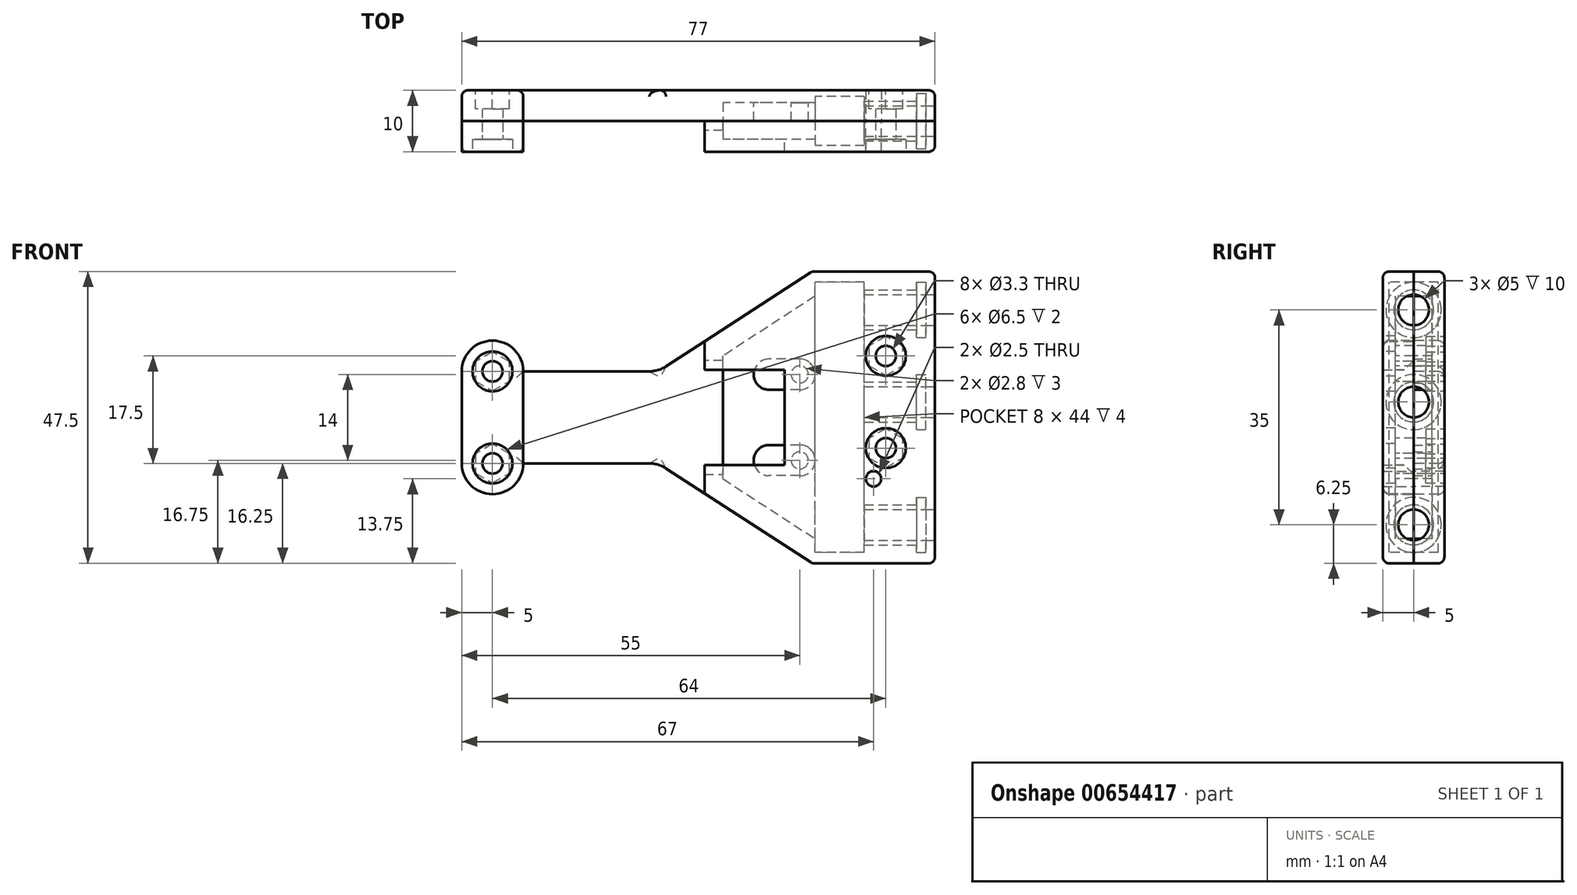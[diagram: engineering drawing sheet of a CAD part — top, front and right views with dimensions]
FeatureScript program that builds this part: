
annotation { "Feature Type Name" : "Feature", "Feature Type Description" : "" }
export const myFeature = defineFeature(function(context is Context, id is Id, definition is map)
    precondition{}
    {
        {
            var Q0;
            Q0=qCreatedBy(makeId("Right.planeOp"),FACE);
            var sketch = newSketch(context, id + "F0", { "sketchPlane" : qUnion([Q0])});
            skCircle(sketch, "E0", {"center": v(0, 17.5) * mm, "radius": 4.5 * mm});
            skCircle(sketch, "E1", {"center": v(0, 17.5) * mm, "radius": 3.25 * mm});
            skCircle(sketch, "E2", {"center": v(0, 2.5) * mm, "radius": 3.25 * mm});
            skCircle(sketch, "E3", {"center": v(0, 2.5) * mm, "radius": 4.5 * mm});
            skCircle(sketch, "E4", {"center": v(0, -17.5) * mm, "radius": 4.5 * mm});
            skCircle(sketch, "E5", {"center": v(0, -17.5) * mm, "radius": 3.25 * mm});
            skCircle(sketch, "E6", {"center": v(0, 17.5) * mm, "radius": 2.5 * mm});
            skCircle(sketch, "E7", {"center": v(0, 2.5) * mm, "radius": 2.5 * mm});
            skCircle(sketch, "E8", {"center": v(0, -17.5) * mm, "radius": 2.5 * mm});
            skLineSegment(sketch, "E9.bottom", {"start": v(5.5, -17.5) * mm, "end": v(-5.5, -17.5) * mm});
            skLineSegment(sketch, "E9.top", {"start": v(5.5, 17.5) * mm, "end": v(-5.5, 17.5) * mm});
            skLineSegment(sketch, "E9.left", {"start": v(5.5, -17.5) * mm, "end": v(5.5, 17.5) * mm});
            skLineSegment(sketch, "E9.right", {"start": v(-5.5, -17.5) * mm, "end": v(-5.5, 17.5) * mm});
            skPoint(sketch, "E9.middle", {"position": v(0, 0) * mm});
            skArc(sketch, "E10", {"start": v(-5.5, 17.5) * mm, "mid": v(0, 23) * mm, "end": v(5.5, 17.5) * mm});
            skArc(sketch, "E11", {"start": v(-5.5, -17.5) * mm, "mid": v(0, -23) * mm, "end": v(5.5, -17.5) * mm});
            skSolve(sketch);
        }
        {
            var Q0;
            {var subQ0=sQuery(id+"F0.wireOp",EDGE,"E9.top");var subQ1=sQuery(id+"F0.wireOp",EDGE,"E1");var subQ2=makeQuery(id+"F0.imprint","INTERSECT",VERTEX,{"disambiguationData":[OD(0.0)],"derivedFrom":[subQ1,subQ0]});Q0=makeQuery(id+"F0.imprint","IMPRINT",FACE,{"disambiguationData":[TD([[makeQuery(id+"F0.imprint","IMPRINT",EDGE,{"disambiguationData":[TD([[subQ2,-1.0]])],"derivedFrom":subQ1}),1.0]])]});}
            var Q1;
            {var subQ0=sQuery(id+"F0.wireOp",EDGE,"E9.top");var subQ1=sQuery(id+"F0.wireOp",EDGE,"E1");var subQ2=makeQuery(id+"F0.imprint","INTERSECT",VERTEX,{"disambiguationData":[OD(0.0)],"derivedFrom":[subQ1,subQ0]});Q1=makeQuery(id+"F0.imprint","IMPRINT",FACE,{"disambiguationData":[TD([[makeQuery(id+"F0.imprint","IMPRINT",EDGE,{"disambiguationData":[TD([[subQ2,1.0]])],"derivedFrom":subQ1}),1.0]])]});}
            var Q2;
            Q2=makeQuery(id+"F0.imprint","IMPRINT",FACE,{"disambiguationData":[TD([[makeQuery(id+"F0.imprint","IMPRINT",EDGE,{"derivedFrom":sQuery(id+"F0.wireOp",EDGE,"E2")}),1.0]])]});
            var Q3;
            {var subQ0=sQuery(id+"F0.wireOp",EDGE,"E9.bottom");var subQ1=sQuery(id+"F0.wireOp",EDGE,"E5");var subQ2=makeQuery(id+"F0.imprint","INTERSECT",VERTEX,{"disambiguationData":[OD(0.0)],"derivedFrom":[subQ1,subQ0]});Q3=makeQuery(id+"F0.imprint","IMPRINT",FACE,{"disambiguationData":[TD([[makeQuery(id+"F0.imprint","IMPRINT",EDGE,{"disambiguationData":[TD([[subQ2,-1.0]])],"derivedFrom":subQ1}),1.0]])]});}
            var Q4;
            {var subQ0=sQuery(id+"F0.wireOp",EDGE,"E9.bottom");var subQ1=sQuery(id+"F0.wireOp",EDGE,"E5");var subQ2=makeQuery(id+"F0.imprint","INTERSECT",VERTEX,{"disambiguationData":[OD(0.0)],"derivedFrom":[subQ1,subQ0]});Q4=makeQuery(id+"F0.imprint","IMPRINT",FACE,{"disambiguationData":[TD([[makeQuery(id+"F0.imprint","IMPRINT",EDGE,{"disambiguationData":[TD([[subQ2,1.0]])],"derivedFrom":subQ1}),1.0]])]});}
            var Q5;
            {var subQ0=sQuery(id+"F0.wireOp",EDGE,"E9.top");var subQ1=sQuery(id+"F0.wireOp",EDGE,"E0");var subQ2=makeQuery(id+"F0.imprint","INTERSECT",VERTEX,{"disambiguationData":[OD(0.0)],"derivedFrom":[subQ1,subQ0]});Q5=makeQuery(id+"F0.imprint","IMPRINT",FACE,{"disambiguationData":[TD([[makeQuery(id+"F0.imprint","IMPRINT",EDGE,{"disambiguationData":[TD([[subQ2,-1.0]])],"derivedFrom":subQ1}),1.0]])]});}
            var Q6;
            {var subQ0=sQuery(id+"F0.wireOp",EDGE,"E9.top");var subQ1=sQuery(id+"F0.wireOp",EDGE,"E0");var subQ2=makeQuery(id+"F0.imprint","INTERSECT",VERTEX,{"disambiguationData":[OD(0.0)],"derivedFrom":[subQ1,subQ0]});Q6=makeQuery(id+"F0.imprint","IMPRINT",FACE,{"disambiguationData":[TD([[makeQuery(id+"F0.imprint","IMPRINT",EDGE,{"disambiguationData":[TD([[subQ2,1.0]])],"derivedFrom":subQ1}),1.0]])]});}
            var Q7;
            Q7=makeQuery(id+"F0.imprint","IMPRINT",FACE,{"disambiguationData":[TD([[makeQuery(id+"F0.imprint","IMPRINT",EDGE,{"derivedFrom":sQuery(id+"F0.wireOp",EDGE,"E2")}),-1.0]])]});
            var Q8;
            {var subQ0=sQuery(id+"F0.wireOp",EDGE,"E9.bottom");var subQ1=sQuery(id+"F0.wireOp",EDGE,"E4");var subQ2=makeQuery(id+"F0.imprint","INTERSECT",VERTEX,{"disambiguationData":[OD(0.0)],"derivedFrom":[subQ1,subQ0]});Q8=makeQuery(id+"F0.imprint","IMPRINT",FACE,{"disambiguationData":[TD([[makeQuery(id+"F0.imprint","IMPRINT",EDGE,{"disambiguationData":[TD([[subQ2,-1.0]])],"derivedFrom":subQ1}),1.0]])]});}
            var Q9;
            {var subQ0=sQuery(id+"F0.wireOp",EDGE,"E9.bottom");var subQ1=sQuery(id+"F0.wireOp",EDGE,"E4");var subQ2=makeQuery(id+"F0.imprint","INTERSECT",VERTEX,{"disambiguationData":[OD(0.0)],"derivedFrom":[subQ1,subQ0]});Q9=makeQuery(id+"F0.imprint","IMPRINT",FACE,{"disambiguationData":[TD([[makeQuery(id+"F0.imprint","IMPRINT",EDGE,{"disambiguationData":[TD([[subQ2,1.0]])],"derivedFrom":subQ1}),1.0]])]});}
            extrude(context, id + "F1", {"entities" : qUnion([Q0, Q1, Q2, Q3, Q4, Q5, Q6, Q7, Q8, Q9]), "oppositeDirection" : true, "depth" : 1.5 * mm, "offsetDistance" : 25 * mm});
        }
        {
            var Q0;
            Q0=makeQuery(id+"F0.imprint","IMPRINT",FACE,{"disambiguationData":[TD([[makeQuery(id+"F0.imprint","IMPRINT",EDGE,{"derivedFrom":sQuery(id+"F0.wireOp",EDGE,"E1")}),1.0]])]});
            var Q1;
            Q1=makeQuery(id+"F0.imprint","IMPRINT",FACE,{"disambiguationData":[TD([[makeQuery(id+"F0.imprint","IMPRINT",EDGE,{"derivedFrom":sQuery(id+"F0.wireOp",EDGE,"E2")}),1.0]])]});
            var Q2;
            Q2=makeQuery(id+"F0.imprint","IMPRINT",FACE,{"disambiguationData":[TD([[makeQuery(id+"F0.imprint","IMPRINT",EDGE,{"derivedFrom":sQuery(id+"F0.wireOp",EDGE,"E5")}),1.0]])]});
            extrude(context, id + "F2", {"entities" : qUnion([Q0, Q1, Q2]), "operationType" : NewBodyOperationType.ADD, "oppositeDirection" : true, "depth" : 15 * mm, "offsetDistance" : 25 * mm});
        }
        {
            var Q0;
            Q0=makeQuery(id+"F2.opExtrude","CAP_FACE",FACE,{"disambiguationData":[OSD([sQuery(id+"F0.wireOp",EDGE,"E1"),sQuery(id+"F0.wireOp",EDGE,"E6")])],"isStart":false});
            var sketch = newSketch(context, id + "F3", { "sketchPlane" : qUnion([Q0])});
            skCircle(sketch, "E12.0", {"center": v(0, 17.5) * mm, "radius": 4.5 * mm});
            skCircle(sketch, "E12.1", {"center": v(0, 17.5) * mm, "radius": 3.25 * mm});
            skCircle(sketch, "E12.2", {"center": v(0, 2.5) * mm, "radius": 4.5 * mm});
            skCircle(sketch, "E12.3", {"center": v(0, 2.5) * mm, "radius": 3.25 * mm});
            skCircle(sketch, "E12.4", {"center": v(0, -17.5) * mm, "radius": 4.5 * mm});
            skCircle(sketch, "E12.5", {"center": v(0, -17.5) * mm, "radius": 3.25 * mm});
            skSolve(sketch);
        }
        {
            var Q0;
            Q0=qCreatedBy(makeId("Front.planeOp"),FACE);
            var sketch = newSketch(context, id + "F4", { "sketchPlane" : qUnion([Q0])});
            skLineSegment(sketch, "E13.left", {"start": v(1.5, -23.75) * mm, "end": v(1.5, 23.75) * mm});
            skLineSegment(sketch, "E14", {"start": v(-77.95, 0) * mm, "end": v(77.95, 0) * mm, "construction": true});
            skPoint(sketch, "E15.orphan", {"position": v(-72.5, 23.75) * mm});
            skLineSegment(sketch, "E16", {"start": v(1.5, 23.75) * mm, "end": v(-18.5, 23.75) * mm});
            skLineSegment(sketch, "E17", {"start": v(-18.5, 23.75) * mm, "end": v(-43.5, 7.5) * mm});
            skLineSegment(sketch, "E18", {"start": v(-43.5, 7.5) * mm, "end": v(-75.5, 7.5) * mm});
            skLineSegment(sketch, "E19.MirrorCS", {"start": v(1.5, -23.75) * mm, "end": v(-18.5, -23.75) * mm});
            skLineSegment(sketch, "E20.MirrorCS", {"start": v(-18.5, -23.75) * mm, "end": v(-43.5, -7.5) * mm});
            skLineSegment(sketch, "E21.MirrorCS", {"start": v(-43.5, -7.5) * mm, "end": v(-75.5, -7.5) * mm});
            skLineSegment(sketch, "E22", {"start": v(-75.5, 7.5) * mm, "end": v(-75.5, -7.5) * mm});
            skLineSegment(sketch, "E23.bottom", {"start": v(-10, -22) * mm, "end": v(-18, -22) * mm});
            skLineSegment(sketch, "E23.top", {"start": v(-10, 22) * mm, "end": v(-18, 22) * mm});
            skLineSegment(sketch, "E23.left", {"start": v(-10, -22) * mm, "end": v(-10, 22) * mm});
            skLineSegment(sketch, "E23.right", {"start": v(-18, -22) * mm, "end": v(-18, 22) * mm});
            skPoint(sketch, "E23.middle", {"position": v(-14, 0) * mm});
            skLineSegment(sketch, "E24.top", {"start": v(-18, 19.75) * mm, "end": v(-33, 10) * mm});
            skLineSegment(sketch, "E24.right", {"start": v(-33, -10) * mm, "end": v(-33, 10) * mm});
            skLineSegment(sketch, "E25.bottom", {"start": v(-23, -7.75) * mm, "end": v(-36, -7.75) * mm});
            skLineSegment(sketch, "E25.top", {"start": v(-23, 7.75) * mm, "end": v(-36, 7.75) * mm});
            skLineSegment(sketch, "E25.left", {"start": v(-23, -7.75) * mm, "end": v(-23, 7.75) * mm});
            skPoint(sketch, "E25.middle", {"position": v(-29.5, 0) * mm});
            skLineSegment(sketch, "E26", {"start": v(-36, -7.75) * mm, "end": v(-36, -12.37) * mm});
            skLineSegment(sketch, "E27", {"start": v(-36, 7.75) * mm, "end": v(-36, 12.37) * mm});
            skLineSegment(sketch, "E28", {"start": v(-18, 19.75) * mm, "end": v(-18, -19.75) * mm});
            skCircle(sketch, "E29", {"center": v(-8.5, -10) * mm, "radius": 1.25 * mm});
            skCircle(sketch, "E30", {"center": v(-70.5, 7.5) * mm, "radius": 5 * mm});
            skCircle(sketch, "E31", {"center": v(-70.5, -7.5) * mm, "radius": 5 * mm});
            skLineSegment(sketch, "E32", {"start": v(-65.5, 7.5) * mm, "end": v(-65.5, -7.5) * mm});
            skLineSegment(sketch, "E33", {"start": v(-33, -10) * mm, "end": v(-18, -19.75) * mm});
            skSolve(sketch);
        }
        {
            var Q0;
            Q0 = qSketchRegion(id + "F4", true);
            var Q1;
            {var subQ5=sQuery(id+"F4.wireOp",EDGE,"E25.left");Q1=makeQuery(id+"F4.imprint","IMPRINT",FACE,{"disambiguationData":[TD([[makeQuery(id+"F4.imprint","IMPRINT",EDGE,{"derivedFrom":subQ5}),1.0]])]});}
            var Q2;
            {var subQ1=sQuery(id+"F4.wireOp",EDGE,"E24.bottom");Q2=makeQuery(id+"F4.imprint","IMPRINT",FACE,{"disambiguationData":[TD([[makeQuery(id+"F4.imprint","IMPRINT",EDGE,{"derivedFrom":subQ1}),-1.0]])]});}
            var Q3;
            {var subQ1=sQuery(id+"F4.wireOp",EDGE,"E23.bottom");Q3=makeQuery(id+"F4.imprint","IMPRINT",FACE,{"disambiguationData":[TD([[makeQuery(id+"F4.imprint","IMPRINT",EDGE,{"derivedFrom":subQ1}),-1.0]])]});}
            var Q4;
            {var subQ4=sQuery(id+"F4.wireOp",EDGE,"E24.top");Q4=makeQuery(id+"F4.imprint","IMPRINT",FACE,{"disambiguationData":[TD([[makeQuery(id+"F4.imprint","IMPRINT",EDGE,{"derivedFrom":subQ4}),1.0]])]});}
            extrude(context, id + "F5", {"entities" : qUnion([Q0, Q1, Q2, Q3, Q4]), "oppositeDirection" : true, "depth" : 5 * mm, "offsetDistance" : 25 * mm});
        }
        {
            var Q0;
            Q0=makeQuery(id+"F5.opExtrude","CAP_FACE",FACE,{"disambiguationData":[OSD([sQuery(id+"F4.wireOp",EDGE,"E13.left"),sQuery(id+"F4.wireOp",EDGE,"E16"),sQuery(id+"F4.wireOp",EDGE,"E17"),sQuery(id+"F4.wireOp",EDGE,"E18"),sQuery(id+"F4.wireOp",EDGE,"E19.MirrorCS"),sQuery(id+"F4.wireOp",EDGE,"E20.MirrorCS"),sQuery(id+"F4.wireOp",EDGE,"E21.MirrorCS"),sQuery(id+"F4.wireOp",EDGE,"E22"),sQuery(id+"F4.wireOp",EDGE,"E29"),sQuery(id+"F4.wireOp",EDGE,"E30"),sQuery(id+"F4.wireOp",EDGE,"E31")])],"isStart":true});
            var sketch = newSketch(context, id + "F6", { "sketchPlane" : qUnion([Q0])});
            skLineSegment(sketch, "E34.0", {"start": v(-75.5, 7.5) * mm, "end": v(-75.5, -7.5) * mm});
            skArc(sketch, "E34.1", {"start": v(-65.5, 7.5) * mm, "mid": v(-70.5, 12.5) * mm, "end": v(-75.5, 7.5) * mm});
            skArc(sketch, "E34.2", {"start": v(-75.5, -7.5) * mm, "mid": v(-70.5, -12.5) * mm, "end": v(-65.5, -7.5) * mm});
            skLineSegment(sketch, "E35", {"start": v(-65.5, 7.5) * mm, "end": v(-65.5, -7.5) * mm});
            skSolve(sketch);
        }
        {
            var Q0;
            Q0 = qSketchRegion(id + "F6", true);
            extrude(context, id + "F7", {"entities" : qUnion([Q0]), "operationType" : NewBodyOperationType.ADD, "depth" : 5 * mm, "offsetDistance" : 25 * mm});
        }
        {
            var Q0;
            Q0=makeQuery(id+"F4.imprint","IMPRINT",FACE,{"disambiguationData":[TD([[makeQuery(id+"F4.imprint","IMPRINT",EDGE,{"derivedFrom":sQuery(id+"F4.wireOp",EDGE,"E13.left")}),1.0]])]});
            var Q1;
            {var subQ1=sQuery(id+"F4.wireOp",EDGE,"E24.bottom");Q1=makeQuery(id+"F4.imprint","IMPRINT",FACE,{"disambiguationData":[TD([[makeQuery(id+"F4.imprint","IMPRINT",EDGE,{"derivedFrom":subQ1}),-1.0]])]});}
            var Q2;
            {var subQ1=sQuery(id+"F4.wireOp",EDGE,"E23.bottom");Q2=makeQuery(id+"F4.imprint","IMPRINT",FACE,{"disambiguationData":[TD([[makeQuery(id+"F4.imprint","IMPRINT",EDGE,{"derivedFrom":subQ1}),-1.0]])]});}
            var Q3;
            {var subQ0=sQuery(id+"F4.wireOp",EDGE,"E30");var subQ1=sQuery(id+"F4.wireOp",EDGE,"E18");var subQ2=makeQuery(id+"F4.imprint","INTERSECT",VERTEX,{"derivedFrom":[subQ1,sQuery(id+"F4.wireOp",EDGE,"E22"),subQ0]});Q3=makeQuery(id+"F4.imprint","IMPRINT",FACE,{"disambiguationData":[TD([[makeQuery(id+"F4.imprint","IMPRINT",EDGE,{"disambiguationData":[TD([[subQ2,1.0]])],"derivedFrom":subQ1}),-1.0]])]});}
            var Q4;
            {var subQ0=sQuery(id+"F4.wireOp",EDGE,"E30");var subQ1=sQuery(id+"F4.wireOp",EDGE,"E18");var subQ2=makeQuery(id+"F4.imprint","INTERSECT",VERTEX,{"derivedFrom":[subQ1,sQuery(id+"F4.wireOp",EDGE,"E22"),subQ0]});Q4=makeQuery(id+"F4.imprint","IMPRINT",FACE,{"disambiguationData":[TD([[makeQuery(id+"F4.imprint","IMPRINT",EDGE,{"disambiguationData":[TD([[subQ2,1.0]])],"derivedFrom":subQ1}),1.0]])]});}
            var Q5;
            {var subQ0=sQuery(id+"F4.wireOp",EDGE,"E22");Q5=makeQuery(id+"F4.imprint","IMPRINT",FACE,{"disambiguationData":[TD([[makeQuery(id+"F4.imprint","IMPRINT",EDGE,{"derivedFrom":subQ0}),1.0]])]});}
            var Q6;
            {var subQ0=sQuery(id+"F4.wireOp",EDGE,"E31");var subQ1=sQuery(id+"F4.wireOp",EDGE,"E21.MirrorCS");var subQ2=makeQuery(id+"F4.imprint","INTERSECT",VERTEX,{"derivedFrom":[subQ1,sQuery(id+"F4.wireOp",EDGE,"E22"),subQ0]});Q6=makeQuery(id+"F4.imprint","IMPRINT",FACE,{"disambiguationData":[TD([[makeQuery(id+"F4.imprint","IMPRINT",EDGE,{"disambiguationData":[TD([[subQ2,1.0]])],"derivedFrom":subQ1}),-1.0]])]});}
            var Q7;
            {var subQ0=sQuery(id+"F4.wireOp",EDGE,"E31");var subQ1=sQuery(id+"F4.wireOp",EDGE,"E21.MirrorCS");var subQ2=makeQuery(id+"F4.imprint","INTERSECT",VERTEX,{"derivedFrom":[subQ1,sQuery(id+"F4.wireOp",EDGE,"E22"),subQ0]});Q7=makeQuery(id+"F4.imprint","IMPRINT",FACE,{"disambiguationData":[TD([[makeQuery(id+"F4.imprint","IMPRINT",EDGE,{"disambiguationData":[TD([[subQ2,1.0]])],"derivedFrom":subQ1}),1.0]])]});}
            var Q8;
            {var subQ4=sQuery(id+"F4.wireOp",EDGE,"E24.top");Q8=makeQuery(id+"F4.imprint","IMPRINT",FACE,{"disambiguationData":[TD([[makeQuery(id+"F4.imprint","IMPRINT",EDGE,{"derivedFrom":subQ4}),1.0]])]});}
            extrude(context, id + "F8", {"entities" : qUnion([Q0, Q1, Q2, Q3, Q4, Q5, Q6, Q7, Q8]), "depth" : 5 * mm, "offsetDistance" : 25 * mm});
        }
        {
            var Q0;
            Q0=makeQuery(id+"F5.opExtrude","SWEPT_FACE",FACE,{"disambiguationData":[OSD([sQuery(id+"F4.wireOp",EDGE,"E13.left")])]});
            var sketch = newSketch(context, id + "F9", { "sketchPlane" : qUnion([Q0])});
            skCircle(sketch, "E36.0", {"center": v(0, 17.5) * mm, "radius": 2.5 * mm});
            skCircle(sketch, "E36.1", {"center": v(0, 2.5) * mm, "radius": 2.5 * mm});
            skCircle(sketch, "E36.2", {"center": v(0, -17.5) * mm, "radius": 2.5 * mm});
            skSolve(sketch);
        }
        {
            var Q0;
            Q0 = qSketchRegion(id + "F9", true);
            var Q1;
            Q1=makeQuery(id+"F2.opExtrude","CAP_FACE",FACE,{"disambiguationData":[OSD([sQuery(id+"F0.wireOp",EDGE,"E1"),sQuery(id+"F0.wireOp",EDGE,"E6")])],"isStart":false});
            extrude(context, id + "F10", {"entities" : qUnion([Q0]), "operationType" : NewBodyOperationType.REMOVE, "endBound" : BoundingType.UP_TO_SURFACE, "oppositeDirection" : true, "depth" : 25 * mm, "endBoundEntityFace" : qUnion([Q1]), "offsetDistance" : 25 * mm});
        }
        {
            var Q0;
            Q0=makeQuery(id+"F9oVLqVhK79UcXx_3.opExtrude","SWEPT_BODY",BODY,{"disambiguationData":[OSD([sQuery(id+"F3.wireOp",EDGE,"E12.0"),sQuery(id+"F3.wireOp",EDGE,"E12.1")])]});
            var Q1;
            Q1=makeQuery(id+"F1.opExtrude","SWEPT_BODY",BODY,{"disambiguationData":[OSD([sQuery(id+"F0.wireOp",EDGE,"E0"),sQuery(id+"F0.wireOp",EDGE,"E6")])]});
            var Q2;
            Q2=makeQuery(id+"F9oVLqVhK79UcXx_3.opExtrude","SWEPT_BODY",BODY,{"disambiguationData":[OSD([sQuery(id+"F3.wireOp",EDGE,"E12.2"),sQuery(id+"F3.wireOp",EDGE,"E12.3")])]});
            var Q3;
            Q3=makeQuery(id+"F1.opExtrude","SWEPT_BODY",BODY,{"disambiguationData":[OSD([sQuery(id+"F0.wireOp",EDGE,"E3"),sQuery(id+"F0.wireOp",EDGE,"E7")])]});
            var Q4;
            Q4=makeQuery(id+"F9oVLqVhK79UcXx_3.opExtrude","SWEPT_BODY",BODY,{"disambiguationData":[OSD([sQuery(id+"F3.wireOp",EDGE,"E12.4"),sQuery(id+"F3.wireOp",EDGE,"E12.5")])]});
            var Q5;
            Q5=makeQuery(id+"F1.opExtrude","SWEPT_BODY",BODY,{"disambiguationData":[OSD([sQuery(id+"F0.wireOp",EDGE,"E4"),sQuery(id+"F0.wireOp",EDGE,"E8")])]});
            var Q6;
            Q6=makeQuery(id+"F5.opExtrude","SWEPT_BODY",BODY,{"disambiguationData":[OSD([sQuery(id+"F4.wireOp",EDGE,"E13.left"),sQuery(id+"F4.wireOp",EDGE,"E16"),sQuery(id+"F4.wireOp",EDGE,"E17"),sQuery(id+"F4.wireOp",EDGE,"E18"),sQuery(id+"F4.wireOp",EDGE,"E19.MirrorCS"),sQuery(id+"F4.wireOp",EDGE,"E20.MirrorCS"),sQuery(id+"F4.wireOp",EDGE,"E21.MirrorCS"),sQuery(id+"F4.wireOp",EDGE,"E22")])]});
            var Q7;
            Q7=makeQuery(id+"F8.opExtrude","SWEPT_BODY",BODY,{"disambiguationData":[OSD([sQuery(id+"F4.wireOp",EDGE,"E13.left"),sQuery(id+"F4.wireOp",EDGE,"E16"),sQuery(id+"F4.wireOp",EDGE,"E17"),sQuery(id+"F4.wireOp",EDGE,"E18"),sQuery(id+"F4.wireOp",EDGE,"E19.MirrorCS"),sQuery(id+"F4.wireOp",EDGE,"E20.MirrorCS"),sQuery(id+"F4.wireOp",EDGE,"E21.MirrorCS"),sQuery(id+"F4.wireOp",EDGE,"E22")])]});
            booleanBodies(context, id + "F11", {"operationType" : BooleanOperationType.SUBTRACTION, "tools" : qUnion([Q0, Q1, Q2, Q3, Q4, Q5]), "targets" : qUnion([Q6, Q7]), "keepTools" : true});
        }
        {
            var Q0;
            {var subQ1=sQuery(id+"F4.wireOp",EDGE,"E23.bottom");Q0=makeQuery(id+"F4.imprint","IMPRINT",FACE,{"disambiguationData":[TD([[makeQuery(id+"F4.imprint","IMPRINT",EDGE,{"derivedFrom":subQ1}),-1.0]])]});}
            extrude(context, id + "F12", {"entities" : qUnion([Q0]), "operationType" : NewBodyOperationType.REMOVE, "endBound" : BoundingType.SYMMETRIC, "oppositeDirection" : true, "depth" : 8 * mm, "offsetDistance" : 25 * mm});
        }
        {
            var Q0;
            {var subQ4=sQuery(id+"F4.wireOp",EDGE,"E24.bottom");Q0=makeQuery(id+"F4.imprint","IMPRINT",FACE,{"disambiguationData":[TD([[makeQuery(id+"F4.imprint","IMPRINT",EDGE,{"derivedFrom":subQ4}),-1.0]])]});}
            var Q1;
            {var subQ5=sQuery(id+"F4.wireOp",EDGE,"E25.left");Q1=makeQuery(id+"F4.imprint","IMPRINT",FACE,{"disambiguationData":[TD([[makeQuery(id+"F4.imprint","IMPRINT",EDGE,{"derivedFrom":subQ5}),1.0]])]});}
            var Q2;
            {var subQ4=sQuery(id+"F4.wireOp",EDGE,"E24.top");Q2=makeQuery(id+"F4.imprint","IMPRINT",FACE,{"disambiguationData":[TD([[makeQuery(id+"F4.imprint","IMPRINT",EDGE,{"derivedFrom":subQ4}),1.0]])]});}
            extrude(context, id + "F13", {"entities" : qUnion([Q0, Q1, Q2]), "operationType" : NewBodyOperationType.REMOVE, "endBound" : BoundingType.SYMMETRIC, "oppositeDirection" : true, "depth" : 6 * mm, "offsetDistance" : 25 * mm});
        }
        {
            var Q0;
            Q0=makeQuery(id+"F5.opExtrude","CAP_FACE",FACE,{"disambiguationData":[OSD([sQuery(id+"F4.wireOp",EDGE,"E13.left"),sQuery(id+"F4.wireOp",EDGE,"E16"),sQuery(id+"F4.wireOp",EDGE,"E17"),sQuery(id+"F4.wireOp",EDGE,"E18"),sQuery(id+"F4.wireOp",EDGE,"E19.MirrorCS"),sQuery(id+"F4.wireOp",EDGE,"E20.MirrorCS"),sQuery(id+"F4.wireOp",EDGE,"E21.MirrorCS"),sQuery(id+"F4.wireOp",EDGE,"E22"),sQuery(id+"F4.wireOp",EDGE,"E29"),sQuery(id+"F4.wireOp",EDGE,"E30"),sQuery(id+"F4.wireOp",EDGE,"E31")])],"isStart":false});
            var sketch = newSketch(context, id + "F14", { "sketchPlane" : qUnion([Q0])});
            skCircle(sketch, "E37.cCircle", {"center": v(6.5, -5) * mm, "radius": 3.18 * mm, "construction": true});
            skLineSegment(sketch, "E37.0", {"start": v(9.25, -3.41) * mm, "end": v(9.25, -6.59) * mm});
            skLineSegment(sketch, "E37.1", {"start": v(9.25, -6.59) * mm, "end": v(6.5, -8.18) * mm});
            skLineSegment(sketch, "E37.2", {"start": v(6.5, -8.18) * mm, "end": v(3.75, -6.59) * mm});
            skLineSegment(sketch, "E37.3", {"start": v(3.75, -6.59) * mm, "end": v(3.75, -3.41) * mm});
            skLineSegment(sketch, "E37.4", {"start": v(3.75, -3.41) * mm, "end": v(6.5, -1.82) * mm});
            skLineSegment(sketch, "E37.5", {"start": v(6.5, -1.82) * mm, "end": v(9.25, -3.41) * mm});
            skCircle(sketch, "E38.cCircle", {"center": v(6.5, 10) * mm, "radius": 3.18 * mm, "construction": true});
            skLineSegment(sketch, "E38.0", {"start": v(9.25, 11.59) * mm, "end": v(9.25, 8.41) * mm});
            skLineSegment(sketch, "E38.1", {"start": v(9.25, 8.41) * mm, "end": v(6.5, 6.82) * mm});
            skLineSegment(sketch, "E38.2", {"start": v(6.5, 6.82) * mm, "end": v(3.75, 8.41) * mm});
            skLineSegment(sketch, "E38.3", {"start": v(3.75, 8.41) * mm, "end": v(3.75, 11.59) * mm});
            skLineSegment(sketch, "E38.4", {"start": v(3.75, 11.59) * mm, "end": v(6.5, 13.18) * mm});
            skLineSegment(sketch, "E38.5", {"start": v(6.5, 13.18) * mm, "end": v(9.25, 11.59) * mm});
            skLineSegment(sketch, "E39", {"start": v(1.76, 2.5) * mm, "end": v(-1.76, 2.5) * mm, "construction": true});
            skCircle(sketch, "E40.cCircle", {"center": v(70.5, -7.5) * mm, "radius": 3.18 * mm, "construction": true});
            skLineSegment(sketch, "E40.0", {"start": v(70.5, -4.32) * mm, "end": v(73.25, -5.91) * mm});
            skLineSegment(sketch, "E40.1", {"start": v(73.25, -5.91) * mm, "end": v(73.25, -9.09) * mm});
            skLineSegment(sketch, "E40.2", {"start": v(73.25, -9.09) * mm, "end": v(70.5, -10.68) * mm});
            skLineSegment(sketch, "E40.3", {"start": v(70.5, -10.68) * mm, "end": v(67.75, -9.09) * mm});
            skLineSegment(sketch, "E40.4", {"start": v(67.75, -9.09) * mm, "end": v(67.75, -5.91) * mm});
            skLineSegment(sketch, "E40.5", {"start": v(67.75, -5.91) * mm, "end": v(70.5, -4.32) * mm});
            skCircle(sketch, "E41.cCircle", {"center": v(70.5, 7.5) * mm, "radius": 3.18 * mm, "construction": true});
            skLineSegment(sketch, "E41.0", {"start": v(73.25, 9.09) * mm, "end": v(73.25, 5.91) * mm});
            skLineSegment(sketch, "E41.1", {"start": v(73.25, 5.91) * mm, "end": v(70.5, 4.32) * mm});
            skLineSegment(sketch, "E41.2", {"start": v(70.5, 4.32) * mm, "end": v(67.75, 5.91) * mm});
            skLineSegment(sketch, "E41.3", {"start": v(67.75, 5.91) * mm, "end": v(67.75, 9.09) * mm});
            skLineSegment(sketch, "E41.4", {"start": v(67.75, 9.09) * mm, "end": v(70.5, 10.68) * mm});
            skLineSegment(sketch, "E41.5", {"start": v(70.5, 10.68) * mm, "end": v(73.25, 9.09) * mm});
            skSolve(sketch);
        }
        {
            var Q0;
            Q0=makeQuery(id+"F8.opExtrude","CAP_FACE",FACE,{"disambiguationData":[OSD([sQuery(id+"F4.wireOp",EDGE,"E13.left"),sQuery(id+"F4.wireOp",EDGE,"E16"),sQuery(id+"F4.wireOp",EDGE,"E17"),sQuery(id+"F4.wireOp",EDGE,"E19.MirrorCS"),sQuery(id+"F4.wireOp",EDGE,"E20.MirrorCS"),sQuery(id+"F4.wireOp",EDGE,"E25.bottom"),sQuery(id+"F4.wireOp",EDGE,"E25.top"),sQuery(id+"F4.wireOp",EDGE,"E25.left"),sQuery(id+"F4.wireOp",EDGE,"E26"),sQuery(id+"F4.wireOp",EDGE,"E27"),sQuery(id+"F4.wireOp",EDGE,"E29")])],"isStart":false});
            var sketch = newSketch(context, id + "F15", { "sketchPlane" : qUnion([Q0])});
            skPoint(sketch, "E42", {"position": v(-6.5, 10) * mm});
            skPoint(sketch, "E43", {"position": v(-6.5, -5) * mm});
            skLineSegment(sketch, "E44", {"start": v(-7.24, 2.5) * mm, "end": v(7.24, 2.5) * mm, "construction": true});
            skPoint(sketch, "E45", {"position": v(-70.5, 7.5) * mm});
            skPoint(sketch, "E46", {"position": v(-70.5, -7.5) * mm});
            skSolve(sketch);
        }
        {
            var Q0;
            Q0 = qSketchRegion(id + "F14", true);
            extrude(context, id + "F16", {"entities" : qUnion([Q0]), "operationType" : NewBodyOperationType.REMOVE, "oppositeDirection" : true, "depth" : 3 * mm, "offsetDistance" : 25 * mm});
        }
        {
            var Q0;
            Q0=sQuery(id+"F15.wireOp",VERTEX,"E42");
            var Q1;
            Q1=sQuery(id+"F15.wireOp",VERTEX,"E43");
            var Q2;
            Q2=sQuery(id+"F15.wireOp",VERTEX,"E45");
            var Q3;
            Q3=sQuery(id+"F15.wireOp",VERTEX,"E46");
            var Q4;
            Q4=makeQuery(id+"F5.opExtrude","SWEPT_BODY",BODY,{"disambiguationData":[OSD([sQuery(id+"F4.wireOp",EDGE,"E13.left"),sQuery(id+"F4.wireOp",EDGE,"E16"),sQuery(id+"F4.wireOp",EDGE,"E17"),sQuery(id+"F4.wireOp",EDGE,"E18"),sQuery(id+"F4.wireOp",EDGE,"E19.MirrorCS"),sQuery(id+"F4.wireOp",EDGE,"E20.MirrorCS"),sQuery(id+"F4.wireOp",EDGE,"E21.MirrorCS"),sQuery(id+"F4.wireOp",EDGE,"E22"),sQuery(id+"F4.wireOp",EDGE,"E29")])]});
            var Q5;
            Q5=makeQuery(id+"F8.opExtrude","SWEPT_BODY",BODY,{"disambiguationData":[OSD([sQuery(id+"F4.wireOp",EDGE,"E13.left"),sQuery(id+"F4.wireOp",EDGE,"E16"),sQuery(id+"F4.wireOp",EDGE,"E17"),sQuery(id+"F4.wireOp",EDGE,"E19.MirrorCS"),sQuery(id+"F4.wireOp",EDGE,"E20.MirrorCS"),sQuery(id+"F4.wireOp",EDGE,"E25.bottom"),sQuery(id+"F4.wireOp",EDGE,"E25.top"),sQuery(id+"F4.wireOp",EDGE,"E25.left"),sQuery(id+"F4.wireOp",EDGE,"E26"),sQuery(id+"F4.wireOp",EDGE,"E27"),sQuery(id+"F4.wireOp",EDGE,"E29")])]});
            var Q6;
            Q6=makeQuery(id+"F8.opExtrude","SWEPT_BODY",BODY,{"disambiguationData":[OSD([sQuery(id+"F4.wireOp",EDGE,"E22"),sQuery(id+"F4.wireOp",EDGE,"E30"),sQuery(id+"F4.wireOp",EDGE,"E31"),sQuery(id+"F4.wireOp",EDGE,"E32")])]});
            hole(context, id + "F17", {"style" : HoleStyle.C_BORE, "endStyle" : HoleEndStyle.THROUGH, "holeDiameter" : 3.3 * mm, "cBoreDiameter" : 6.5 * mm, "cBoreDepth" : 2 * mm, "majorDiameter" : 5 * mm, "isTappedThrough" : true, "tappedDepth" : 12 * mm, "tapClearance" : 3, "locations" : qUnion([Q0, Q1, Q2, Q3]), "scope" : qUnion([Q4, Q5, Q6])});
        }
        {
            var Q0;
            Q0=makeQuery(id+"F5.opExtrude","CAP_EDGE",EDGE,{"disambiguationData":[OSD([sQuery(id+"F4.wireOp",EDGE,"E16")])],"isStart":false});
            var Q1;
            Q1=makeQuery(id+"F5.opExtrude","CAP_EDGE",EDGE,{"disambiguationData":[OSD([sQuery(id+"F4.wireOp",EDGE,"E17")])],"isStart":false});
            var Q2;
            Q2=makeQuery(id+"F5.opExtrude","CAP_EDGE",EDGE,{"disambiguationData":[OSD([sQuery(id+"F4.wireOp",EDGE,"E18")])],"isStart":false});
            var Q3;
            Q3=makeQuery(id+"F5.opExtrude","CAP_EDGE",EDGE,{"disambiguationData":[OSD([sQuery(id+"F4.wireOp",EDGE,"E30")])],"isStart":false});
            var Q4;
            Q4=makeQuery(id+"F5.opExtrude","CAP_EDGE",EDGE,{"disambiguationData":[OSD([sQuery(id+"F4.wireOp",EDGE,"E21.MirrorCS")])],"isStart":false});
            var Q5;
            Q5=makeQuery(id+"F5.opExtrude","CAP_EDGE",EDGE,{"disambiguationData":[OSD([sQuery(id+"F4.wireOp",EDGE,"E20.MirrorCS")])],"isStart":false});
            var Q6;
            Q6=makeQuery(id+"F5.opExtrude","CAP_EDGE",EDGE,{"disambiguationData":[OSD([sQuery(id+"F4.wireOp",EDGE,"E19.MirrorCS")])],"isStart":false});
            var Q7;
            Q7=makeQuery(id+"F5.opExtrude","SWEPT_EDGE",EDGE,{"disambiguationData":[OSD([sQuery(id+"F4.wireOp",EDGE,"E16"),sQuery(id+"F4.wireOp",EDGE,"E17")])]});
            var Q8;
            Q8=makeQuery(id+"F8.opExtrude","SWEPT_EDGE",EDGE,{"disambiguationData":[OSD([sQuery(id+"F4.wireOp",EDGE,"E16"),sQuery(id+"F4.wireOp",EDGE,"E17")])]});
            var Q9;
            Q9=makeQuery(id+"F5.opExtrude","SWEPT_EDGE",EDGE,{"disambiguationData":[OSD([sQuery(id+"F4.wireOp",EDGE,"E19.MirrorCS"),sQuery(id+"F4.wireOp",EDGE,"E20.MirrorCS")])]});
            var Q10;
            Q10=makeQuery(id+"F8.opExtrude","SWEPT_EDGE",EDGE,{"disambiguationData":[OSD([sQuery(id+"F4.wireOp",EDGE,"E19.MirrorCS"),sQuery(id+"F4.wireOp",EDGE,"E20.MirrorCS")])]});
            var Q11;
            Q11=makeQuery(id+"F8.opExtrude","CAP_EDGE",EDGE,{"disambiguationData":[OSD([sQuery(id+"F4.wireOp",EDGE,"E19.MirrorCS")])],"isStart":false});
            var Q12;
            Q12=makeQuery(id+"F8.opExtrude","CAP_EDGE",EDGE,{"disambiguationData":[OSD([sQuery(id+"F4.wireOp",EDGE,"E20.MirrorCS")])],"isStart":false});
            var Q13;
            Q13=makeQuery(id+"F8.opExtrude","CAP_EDGE",EDGE,{"disambiguationData":[OSD([sQuery(id+"F4.wireOp",EDGE,"E17")])],"isStart":false});
            var Q14;
            Q14=makeQuery(id+"F8.opExtrude","CAP_EDGE",EDGE,{"disambiguationData":[OSD([sQuery(id+"F4.wireOp",EDGE,"E16")])],"isStart":false});
            var Q15;
            Q15=makeQuery(id+"F8.opExtrude","CAP_EDGE",EDGE,{"disambiguationData":[OSD([sQuery(id+"F4.wireOp",EDGE,"E30")])],"isStart":false});
            var Q16;
            Q16=makeQuery(id+"F8.opExtrude","CAP_EDGE",EDGE,{"disambiguationData":[OSD([sQuery(id+"F4.wireOp",EDGE,"E32")])],"isStart":false});
            var Q17;
            Q17=makeQuery(id+"F8.opExtrude","SWEPT_EDGE",EDGE,{"disambiguationData":[OSD([sQuery(id+"F4.wireOp",EDGE,"E13.left"),sQuery(id+"F4.wireOp",EDGE,"E16")])]});
            var Q18;
            Q18=makeQuery(id+"F5.opExtrude","SWEPT_EDGE",EDGE,{"disambiguationData":[OSD([sQuery(id+"F4.wireOp",EDGE,"E13.left"),sQuery(id+"F4.wireOp",EDGE,"E16")])]});
            var Q19;
            Q19=makeQuery(id+"F8.opExtrude","CAP_EDGE",EDGE,{"disambiguationData":[OSD([sQuery(id+"F4.wireOp",EDGE,"E13.left")])],"isStart":false});
            var Q20;
            Q20=makeQuery(id+"F5.opExtrude","CAP_EDGE",EDGE,{"disambiguationData":[OSD([sQuery(id+"F4.wireOp",EDGE,"E13.left")])],"isStart":false});
            var Q21;
            Q21=makeQuery(id+"F8.opExtrude","SWEPT_EDGE",EDGE,{"disambiguationData":[OSD([sQuery(id+"F4.wireOp",EDGE,"E13.left"),sQuery(id+"F4.wireOp",EDGE,"E19.MirrorCS")])]});
            var Q22;
            Q22=makeQuery(id+"F5.opExtrude","SWEPT_EDGE",EDGE,{"disambiguationData":[OSD([sQuery(id+"F4.wireOp",EDGE,"E13.left"),sQuery(id+"F4.wireOp",EDGE,"E19.MirrorCS")])]});
            fillet(context, id + "F18", {"entities" : qUnion([Q0, Q1, Q2, Q3, Q4, Q5, Q6, Q7, Q8, Q9, Q10, Q11, Q12, Q13, Q14, Q15, Q16, Q17, Q18, Q19, Q20, Q21, Q22]), "radius" : 1 * mm, "tangentPropagation" : true, "allowEdgeOverflow" : false});
        }
        {
            var Q0;
            Q0=makeQuery(id+"F5.opExtrude","SWEPT_EDGE",EDGE,{"disambiguationData":[OSD([sQuery(id+"F4.wireOp",EDGE,"E17"),sQuery(id+"F4.wireOp",EDGE,"E18")])]});
            var Q1;
            Q1=makeQuery(id+"F5.opExtrude","SWEPT_EDGE",EDGE,{"disambiguationData":[OSD([sQuery(id+"F4.wireOp",EDGE,"E20.MirrorCS"),sQuery(id+"F4.wireOp",EDGE,"E21.MirrorCS")])]});
            fillet(context, id + "F19", {"entities" : qUnion([Q0, Q1]), "radius" : 5 * mm, "tangentPropagation" : true, "allowEdgeOverflow" : false});
        }
        {
            var Q0;
            Q0=makeQuery(id+"F8.opExtrude","CAP_EDGE",EDGE,{"disambiguationData":[OSD([sQuery(id+"F4.wireOp",EDGE,"E25.top")])],"isStart":true});
            var Q1;
            Q1=makeQuery(id+"F8.opExtrude","CAP_EDGE",EDGE,{"disambiguationData":[OSD([sQuery(id+"F4.wireOp",EDGE,"E25.bottom")])],"isStart":true});
            chamfer(context, id + "F20", {"entities" : qUnion([Q0, Q1]), "width" : 1.5 * mm, "tangentPropagation" : true});
        }
        {
            var Q0;
            Q0=makeQuery(id+"F13.boolean.opBoolean","COPY",FACE,{"derivedFrom":makeQuery(id+"F13.opExtrude","CAP_FACE",FACE,{"disambiguationData":[OSD([sQuery(id+"F4.wireOp",EDGE,"E24.top"),sQuery(id+"F4.wireOp",EDGE,"E24.right"),sQuery(id+"F4.wireOp",EDGE,"E28"),sQuery(id+"F4.wireOp",EDGE,"E33")])],"isStart":false})});
            var sketch = newSketch(context, id + "F21", { "sketchPlane" : qUnion([Q0])});
            skLineSegment(sketch, "E47.bottom", {"start": v(-20.5, 9.5) * mm, "end": v(-25.5, 9.5) * mm});
            skLineSegment(sketch, "E47.top", {"start": v(-20.5, 4.5) * mm, "end": v(-25.5, 4.5) * mm});
            skArc(sketch, "E48", {"start": v(-20.5, 9.5) * mm, "mid": v(-18, 7) * mm, "end": v(-20.5, 4.5) * mm});
            skArc(sketch, "E49", {"start": v(-25.5, 9.5) * mm, "mid": v(-28, 7) * mm, "end": v(-25.5, 4.5) * mm});
            skArc(sketch, "E50.MirrorCS", {"start": v(-20.5, -9.5) * mm, "mid": v(-18, -7) * mm, "end": v(-20.5, -4.5) * mm});
            skLineSegment(sketch, "E51.MirrorCS", {"start": v(-20.5, -9.5) * mm, "end": v(-25.5, -9.5) * mm});
            skArc(sketch, "E52.MirrorCS", {"start": v(-25.5, -9.5) * mm, "mid": v(-28, -7) * mm, "end": v(-25.5, -4.5) * mm});
            skLineSegment(sketch, "E53.MirrorCS", {"start": v(-20.5, -4.5) * mm, "end": v(-25.5, -4.5) * mm});
            skSolve(sketch);
        }
        {
            var Q0;
            Q0 = qSketchRegion(id + "F21", true);
            var Q1;
            {var subQ0=sQuery(id+"F0.wireOp",EDGE,"E4");var subQ1=makeQuery(id+"F1.opExtrude","SWEPT_FACE",FACE,{"disambiguationData":[OSD([subQ0])]});var subQ2=sQuery(id+"F4.wireOp",EDGE,"E13.left");var subQ3=makeQuery(id+"F5.opExtrude","SWEPT_FACE",FACE,{"disambiguationData":[OSD([subQ2])]});var subQ4=sQuery(id+"F4.wireOp",EDGE,"E31");var subQ5=sQuery(id+"F4.wireOp",EDGE,"E30");var subQ6=sQuery(id+"F4.wireOp",EDGE,"E22");var subQ7=sQuery(id+"F4.wireOp",EDGE,"E21.MirrorCS");var subQ8=sQuery(id+"F4.wireOp",EDGE,"E20.MirrorCS");var subQ9=sQuery(id+"F4.wireOp",EDGE,"E19.MirrorCS");var subQ10=sQuery(id+"F4.wireOp",EDGE,"E18");var subQ11=sQuery(id+"F4.wireOp",EDGE,"E17");var subQ12=sQuery(id+"F4.wireOp",EDGE,"E16");var subQ13=makeQuery(id+"F5.opExtrude","CAP_FACE",FACE,{"disambiguationData":[OSD([subQ2,subQ12,subQ11,subQ10,subQ9,subQ8,subQ7,subQ6,sQuery(id+"F4.wireOp",EDGE,"E29"),subQ5,subQ4])],"isStart":true});var subQ14=sQuery(id+"F0.wireOp",EDGE,"E6");var subQ15=sQuery(id+"F0.wireOp",EDGE,"E1");var subQ17=makeQuery(id+"F10.opExtrude","SWEPT_FACE",FACE,{"disambiguationData":[OSD([sQuery(id+"F9.wireOp",EDGE,"E36.2")])]});var subQ18=makeQuery(id+"F10.boolean.opBoolean","COPY",FACE,{"disambiguationData":[TD([subQ3])],"derivedFrom":subQ17});var subQ19=sQuery(id+"F0.wireOp",EDGE,"E8");var subQ20=makeQuery(id+"F1.opExtrude","CAP_FACE",FACE,{"disambiguationData":[OSD([subQ0,subQ19])],"isStart":true});var subQ21=makeQuery(id+"F1.opExtrude","CAP_FACE",FACE,{"disambiguationData":[OSD([subQ0,subQ19])],"isStart":false});var subQ22=sQuery(id+"F0.wireOp",EDGE,"E5");var subQ23=makeQuery(id+"F2.opExtrude","SWEPT_FACE",FACE,{"disambiguationData":[OSD([subQ22])]});var subQ24=sQuery(id+"F0.wireOp",EDGE,"E0");var subQ25=makeQuery(id+"F1.opExtrude","CAP_FACE",FACE,{"disambiguationData":[OSD([subQ24,subQ14])],"isStart":false});var subQ26=makeQuery(id+"F10.opExtrude","SWEPT_FACE",FACE,{"disambiguationData":[OSD([sQuery(id+"F9.wireOp",EDGE,"E36.0")])]});var subQ28=makeQuery(id+"F2.opExtrude","SWEPT_FACE",FACE,{"disambiguationData":[OSD([subQ15])]});var subQ29=makeQuery(id+"F1.opExtrude","CAP_FACE",FACE,{"disambiguationData":[OSD([subQ24,subQ14])],"isStart":true});var subQ30=makeQuery(id+"F1.opExtrude","SWEPT_FACE",FACE,{"disambiguationData":[OSD([subQ24])]});var subQ31=makeQuery(id+"F10.boolean.opBoolean","COPY",FACE,{"disambiguationData":[TD([subQ3])],"derivedFrom":subQ26});Q1=makeQuery(id+"F12.boolean.opBoolean","SPLIT",FACE,{"disambiguationData":[TD([subQ3,makeQuery(id+"F5.opExtrude","SWEPT_FACE",FACE,{"disambiguationData":[OSD([subQ12])]}),makeQuery(id+"F5.opExtrude","SWEPT_FACE",FACE,{"disambiguationData":[OSD([subQ11])]}),makeQuery(id+"F5.opExtrude","SWEPT_FACE",FACE,{"disambiguationData":[OSD([subQ10])]}),makeQuery(id+"F5.opExtrude","SWEPT_FACE",FACE,{"disambiguationData":[OSD([subQ9])]}),makeQuery(id+"F5.opExtrude","SWEPT_FACE",FACE,{"disambiguationData":[OSD([subQ8])]}),makeQuery(id+"F5.opExtrude","SWEPT_FACE",FACE,{"disambiguationData":[OSD([subQ7])]}),makeQuery(id+"F5.opExtrude","SWEPT_FACE",FACE,{"disambiguationData":[OSD([subQ6])]}),makeQuery(id+"F5.opExtrude","SWEPT_FACE",FACE,{"disambiguationData":[OSD([subQ5])]}),makeQuery(id+"F5.opExtrude","SWEPT_FACE",FACE,{"disambiguationData":[OSD([subQ4])]}),subQ31,subQ18,makeQuery(id+"F11.opBoolean","COPY",FACE,{"disambiguationData":[TD([subQ13])],"derivedFrom":subQ30}),makeQuery(id+"F11.opBoolean","COPY",FACE,{"disambiguationData":[TD([subQ13])],"derivedFrom":subQ1}),makeQuery(id+"F11.opBoolean","COPY",FACE,{"disambiguationData":[TD([subQ13])],"derivedFrom":subQ29}),makeQuery(id+"F11.opBoolean","COPY",FACE,{"disambiguationData":[TD([subQ13])],"derivedFrom":subQ25}),makeQuery(id+"F11.opBoolean","COPY",FACE,{"disambiguationData":[TD([subQ13])],"derivedFrom":subQ20}),makeQuery(id+"F11.opBoolean","COPY",FACE,{"disambiguationData":[TD([subQ13])],"derivedFrom":subQ21}),makeQuery(id+"F11.opBoolean","COPY",FACE,{"disambiguationData":[TD([subQ13])],"derivedFrom":subQ28}),makeQuery(id+"F11.opBoolean","COPY",FACE,{"disambiguationData":[TD([subQ13])],"derivedFrom":subQ23}),makeQuery(id+"F12.opExtrude","SWEPT_FACE",FACE,{"disambiguationData":[OSD([sQuery(id+"F4.wireOp",EDGE,"E23.bottom")])]}),makeQuery(id+"F12.opExtrude","SWEPT_FACE",FACE,{"disambiguationData":[OSD([sQuery(id+"F4.wireOp",EDGE,"E23.top")])]}),makeQuery(id+"F12.opExtrude","SWEPT_FACE",FACE,{"disambiguationData":[OSD([sQuery(id+"F4.wireOp",EDGE,"E23.left")])]}),makeQuery(id+"F12.opExtrude","SWEPT_FACE",FACE,{"disambiguationData":[OSD([sQuery(id+"F4.wireOp",EDGE,"E23.right"),sQuery(id+"F4.wireOp",EDGE,"E28")])]})])],"derivedFrom":subQ13});}
            extrude(context, id + "F22", {"entities" : qUnion([Q0]), "operationType" : NewBodyOperationType.ADD, "endBound" : BoundingType.UP_TO_SURFACE, "depth" : 25 * mm, "endBoundEntityFace" : qUnion([Q1]), "offsetDistance" : 25 * mm});
        }
        {
            var Q0;
            Q0=sQuery(id+"F21.wireOp",VERTEX,"E48.center");
            var Q1;
            Q1=sQuery(id+"F21.wireOp",VERTEX,"E50.MirrorCS.center");
            var Q2;
            Q2=makeQuery(id+"F5.opExtrude","SWEPT_BODY",BODY,{"disambiguationData":[OSD([sQuery(id+"F4.wireOp",EDGE,"E13.left"),sQuery(id+"F4.wireOp",EDGE,"E16"),sQuery(id+"F4.wireOp",EDGE,"E17"),sQuery(id+"F4.wireOp",EDGE,"E18"),sQuery(id+"F4.wireOp",EDGE,"E19.MirrorCS"),sQuery(id+"F4.wireOp",EDGE,"E20.MirrorCS"),sQuery(id+"F4.wireOp",EDGE,"E21.MirrorCS"),sQuery(id+"F4.wireOp",EDGE,"E22"),sQuery(id+"F4.wireOp",EDGE,"E29"),sQuery(id+"F4.wireOp",EDGE,"E30"),sQuery(id+"F4.wireOp",EDGE,"E31")])]});
            hole(context, id + "F23", {"style" : HoleStyle.SIMPLE, "endStyle" : HoleEndStyle.THROUGH, "oppositeDirection" : true, "holeDiameter" : 2.8 * mm, "majorDiameter" : 3 * mm, "isTappedThrough" : true, "tappedDepth" : 12 * mm, "tapClearance" : 3, "locations" : qUnion([Q0, Q1]), "scope" : qUnion([Q2])});
        }
    });
